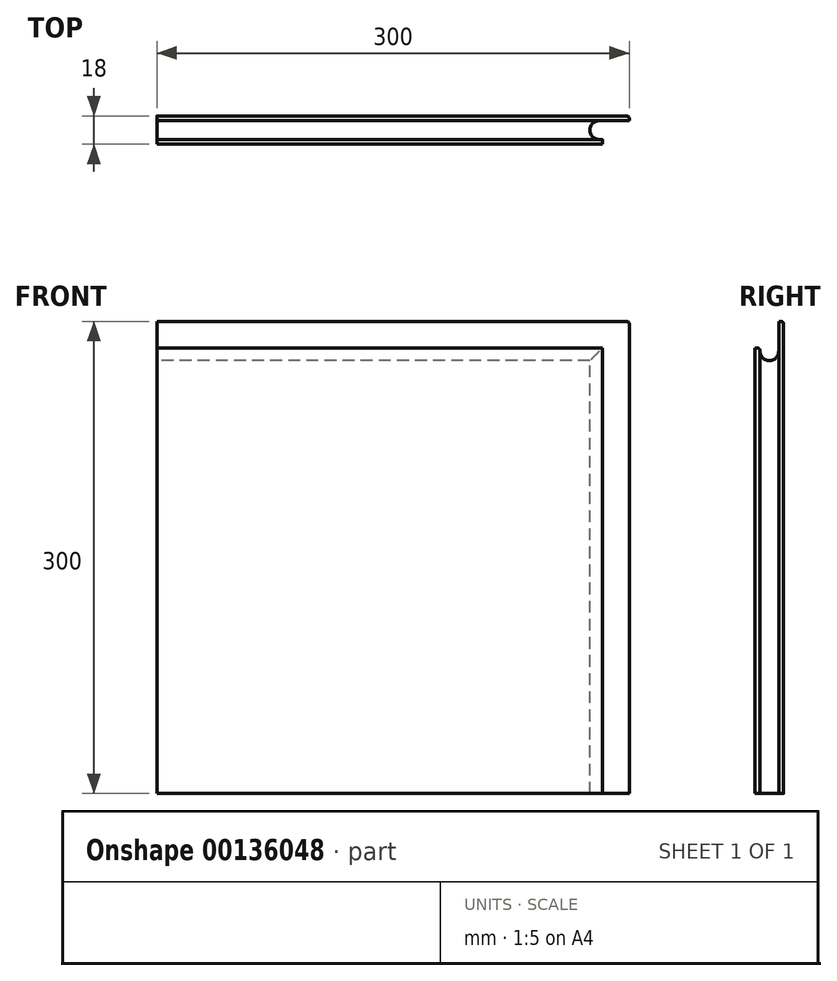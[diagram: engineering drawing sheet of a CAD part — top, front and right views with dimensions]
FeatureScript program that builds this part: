
annotation { "Feature Type Name" : "Feature", "Feature Type Description" : "" }
export const myFeature = defineFeature(function(context is Context, id is Id, definition is map)
    precondition{}
    {
        {
            var Q0;
            Q0=qCreatedBy(makeId("Front.planeOp"),FACE);
            var sketch = newSketch(context, id + "F0", { "sketchPlane" : qUnion([Q0])});
            skLineSegment(sketch, "E0.bottom", {"start": v(-153.72, 144.22) * mm, "end": v(146.28, 144.22) * mm});
            skLineSegment(sketch, "E0.top", {"start": v(-153.72, -155.78) * mm, "end": v(146.28, -155.78) * mm});
            skLineSegment(sketch, "E0.left", {"start": v(-153.72, 144.22) * mm, "end": v(-153.72, -155.78) * mm});
            skLineSegment(sketch, "E0.right", {"start": v(146.28, 144.22) * mm, "end": v(146.28, -155.78) * mm});
            skSolve(sketch);
        }
        {
            var Q0;
            Q0=makeQuery(id+"F0.imprint","IMPRINT",FACE,{"disambiguationData":[TD([[makeQuery(id+"F0.imprint","IMPRINT",EDGE,{"derivedFrom":sQuery(id+"F0.wireOp",EDGE,"E0.bottom")}),-1.0]])]});
            extrude(context, id + "F1", {"entities" : qUnion([Q0]), "endBound" : BoundingType.SYMMETRIC, "depth" : 18 * mm});
        }
        {
            var Q0;
            Q0=makeQuery(id+"F1.opExtrude","SWEPT_FACE",FACE,{"disambiguationData":[OSD([sQuery(id+"F0.wireOp",EDGE,"E0.right")])]});
            var sketch = newSketch(context, id + "F2", { "sketchPlane" : qUnion([Q0])});
            skLineSegment(sketch, "E1", {"start": v(-9, 144.22) * mm, "end": v(6, 144.22) * mm});
            skLineSegment(sketch, "E2", {"start": v(6, 144.22) * mm, "end": v(6, 119.22) * mm});
            skLineSegment(sketch, "E3", {"start": v(6, 119.22) * mm, "end": v(-6, 119.22) * mm});
            skLineSegment(sketch, "E4", {"start": v(-6, 119.22) * mm, "end": v(-6, 127.22) * mm});
            skLineSegment(sketch, "E5", {"start": v(-6, 127.22) * mm, "end": v(-9, 127.22) * mm});
            skLineSegment(sketch, "E6", {"start": v(-9, 127.22) * mm, "end": v(-9, 144.22) * mm});
            skSolve(sketch);
        }
        {
            var Q0;
            Q0=makeQuery(id+"F2.imprint","IMPRINT",FACE,{"disambiguationData":[TD([[makeQuery(id+"F2.imprint","IMPRINT",EDGE,{"derivedFrom":sQuery(id+"F2.wireOp",EDGE,"E1")}),-1.0]])]});
            extrude(context, id + "F3", {"entities" : qUnion([Q0]), "operationType" : NewBodyOperationType.REMOVE, "endBound" : BoundingType.THROUGH_ALL, "oppositeDirection" : true, "depth" : 25 * mm});
        }
        {
            var Q0;
            Q0=makeQuery(id+"F3.boolean.opBoolean","COPY",EDGE,{"derivedFrom":makeQuery(id+"F3.opExtrude","SWEPT_EDGE",EDGE,{"disambiguationData":[OSD([sQuery(id+"F0.wireOp",EDGE,"E0.bottom"),sQuery(id+"F0.wireOp",EDGE,"E0.right"),sQuery(id+"F2.wireOp",EDGE,"E1"),sQuery(id+"F2.wireOp",EDGE,"E2")])]})});
            var Q1;
            Q1=makeQuery(id+"F1.opExtrude","CAP_EDGE",EDGE,{"disambiguationData":[OSD([sQuery(id+"F0.wireOp",EDGE,"E0.bottom")])],"isStart":true});
            var Q2;
            Q2=makeQuery(id+"F3.boolean.opBoolean","COPY",EDGE,{"derivedFrom":makeQuery(id+"F3.opExtrude","SWEPT_EDGE",EDGE,{"disambiguationData":[OSD([sQuery(id+"F0.wireOp",EDGE,"E0.right"),sQuery(id+"F2.wireOp",EDGE,"E5"),sQuery(id+"F2.wireOp",EDGE,"E6")])]})});
            var Q3;
            Q3=makeQuery(id+"F3.boolean.opBoolean","COPY",EDGE,{"derivedFrom":makeQuery(id+"F3.opExtrude","SWEPT_EDGE",EDGE,{"disambiguationData":[OSD([sQuery(id+"F2.wireOp",EDGE,"E4"),sQuery(id+"F2.wireOp",EDGE,"E5")])]})});
            fillet(context, id + "F4", {"entities" : qUnion([Q0, Q1, Q2, Q3]), "radius" : 1.5 * mm, "tangentPropagation" : true, "allowEdgeOverflow" : false});
        }
        {
            var Q0;
            Q0=makeQuery(id+"F3.boolean.opBoolean","COPY",EDGE,{"derivedFrom":makeQuery(id+"F3.opExtrude","SWEPT_EDGE",EDGE,{"disambiguationData":[OSD([sQuery(id+"F2.wireOp",EDGE,"E2"),sQuery(id+"F2.wireOp",EDGE,"E3")])]})});
            var Q1;
            Q1=makeQuery(id+"F3.boolean.opBoolean","COPY",EDGE,{"derivedFrom":makeQuery(id+"F3.opExtrude","SWEPT_EDGE",EDGE,{"disambiguationData":[OSD([sQuery(id+"F2.wireOp",EDGE,"E3"),sQuery(id+"F2.wireOp",EDGE,"E4")])]})});
            fillet(context, id + "F5", {"entities" : qUnion([Q0, Q1]), "radius" : 6 * mm, "tangentPropagation" : true, "allowEdgeOverflow" : false});
        }
        {
            var Q0;
            Q0=makeQuery(id+"F1.opExtrude","SWEPT_FACE",FACE,{"disambiguationData":[OSD([sQuery(id+"F0.wireOp",EDGE,"E0.top")])]});
            var sketch = newSketch(context, id + "F6", { "sketchPlane" : qUnion([Q0])});
            skLineSegment(sketch, "E7", {"start": v(146.28, 9) * mm, "end": v(146.28, -6) * mm});
            skLineSegment(sketch, "E8", {"start": v(146.28, -6) * mm, "end": v(121.28, -6) * mm});
            skLineSegment(sketch, "E9", {"start": v(121.28, -6) * mm, "end": v(121.28, 6) * mm});
            skLineSegment(sketch, "E10", {"start": v(121.28, 6) * mm, "end": v(129.28, 6) * mm});
            skLineSegment(sketch, "E11", {"start": v(129.28, 6) * mm, "end": v(129.28, 9) * mm});
            skLineSegment(sketch, "E12", {"start": v(129.28, 9) * mm, "end": v(146.28, 9) * mm});
            skSolve(sketch);
        }
        {
            var Q0;
            Q0=makeQuery(id+"F6.imprint","IMPRINT",FACE,{"disambiguationData":[TD([[makeQuery(id+"F6.imprint","IMPRINT",EDGE,{"derivedFrom":sQuery(id+"F6.wireOp",EDGE,"E7")}),-1.0]])]});
            extrude(context, id + "F7", {"entities" : qUnion([Q0]), "operationType" : NewBodyOperationType.REMOVE, "endBound" : BoundingType.THROUGH_ALL, "oppositeDirection" : true, "depth" : 25 * mm});
        }
        {
            var Q0;
            Q0=makeQuery(id+"F7.boolean.opBoolean","COPY",EDGE,{"derivedFrom":makeQuery(id+"F7.opExtrude","SWEPT_EDGE",EDGE,{"disambiguationData":[OSD([sQuery(id+"F6.wireOp",EDGE,"E8"),sQuery(id+"F6.wireOp",EDGE,"E9")])]})});
            var Q1;
            Q1=makeQuery(id+"F7.boolean.opBoolean","COPY",EDGE,{"derivedFrom":makeQuery(id+"F7.opExtrude","SWEPT_EDGE",EDGE,{"disambiguationData":[OSD([sQuery(id+"F6.wireOp",EDGE,"E9"),sQuery(id+"F6.wireOp",EDGE,"E10")])]})});
            fillet(context, id + "F8", {"entities" : qUnion([Q0, Q1]), "radius" : 6 * mm, "tangentPropagation" : true, "allowEdgeOverflow" : false});
        }
        {
            var Q0;
            Q0=makeQuery(id+"F7.boolean.opBoolean","COPY",EDGE,{"derivedFrom":makeQuery(id+"F7.opExtrude","SWEPT_EDGE",EDGE,{"disambiguationData":[OSD([sQuery(id+"F6.wireOp",EDGE,"E10"),sQuery(id+"F6.wireOp",EDGE,"E11")])]})});
            var Q1;
            Q1=makeQuery(id+"F1.opExtrude","CAP_EDGE",EDGE,{"disambiguationData":[OSD([sQuery(id+"F0.wireOp",EDGE,"E0.right")])],"isStart":true});
            fillet(context, id + "F9", {"entities" : qUnion([Q0, Q1]), "radius" : 1.5 * mm, "tangentPropagation" : true, "allowEdgeOverflow" : false});
        }
    });
